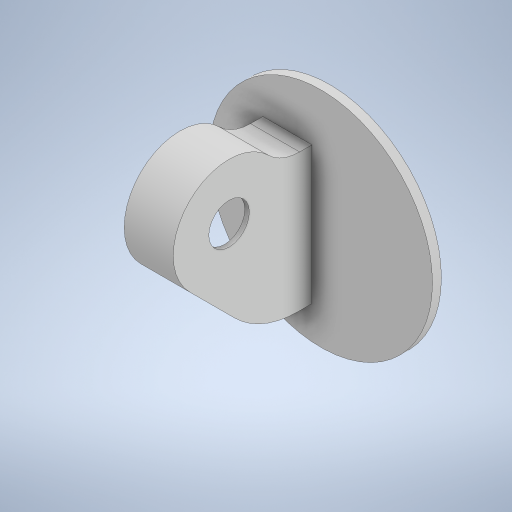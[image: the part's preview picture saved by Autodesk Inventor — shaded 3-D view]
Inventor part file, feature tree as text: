
AUTODESK INVENTOR PART (.ipt)
format: ipt  version: 2024.1 (Build 281209000, 209)  size: 322,560 bytes
history: native  units: in
note: dims shown in document units (in); Inventor stores cm internally (conversion verified against a paired STEP export)
features: extrude x5, sketch x5, fillet x2, plane x1
ambient origin geometry x8: Origin, YZ Plane, XZ Plane, XY Plane, X Axis, Y Axis, Z Axis, Center Point
bodies: Solid1 (feature_tree)
feature tree (13):
  extrude  "Extrusion1"  Depth=0.3937in TaperAngle=0.0deg
  plane  "Work Plane1"
  extrude  "Extrusion2"  Depth=3.4449in
  fillet  "Fillet1"  Radius=2.6181in
  fillet  "Fillet2"  Radius=1.3583in
  extrude  "Extrusion3"  TaperAngle=45.0deg  [1 undecoded]
  extrude  "Extrusion4"  TaperAngle=135.0deg  [1 undecoded]
  extrude  "Extrusion5"  Depth=2.1654in TaperAngle=0.0deg
  sketch  "Sketch1"  dims[d0=9.8425in d1=0.3937in d2=0.0in]
  sketch  "Sketch2"  dims[d3=-0.3937in d4=3.4449in d6=2.6181in d7=1.3583in]
  sketch  "Sketch3"  dims[d8=0.7874in d9=45.0deg]
  sketch  "Sketch4"  dims[d10=4.9213in d11=135.0deg]
  sketch  "Sketch5"  dims[d12=1.7913in d13=2.1654in d14=0.0in d16=0.3937in d17=2.5591in d18=0.3937in d19=1.5748in d20=3.937in d21=1.9685in d22=0.7677in d23=0.0in d24=1.0492in d25=1.0492in d26=1.0492in d27=4.0945in d28=1.1969in d29=0.0in d30=0.3504in d31=0.2598in d32=0.2598in d33=0.3661in d34=0.3661in d35=0.748in d36=0.0in]
note: 2 required parameter values undecoded (feature->parameter linkage not recoverable at this tier; creation-order binding heuristic only, values carry confidence <= 0.55)
